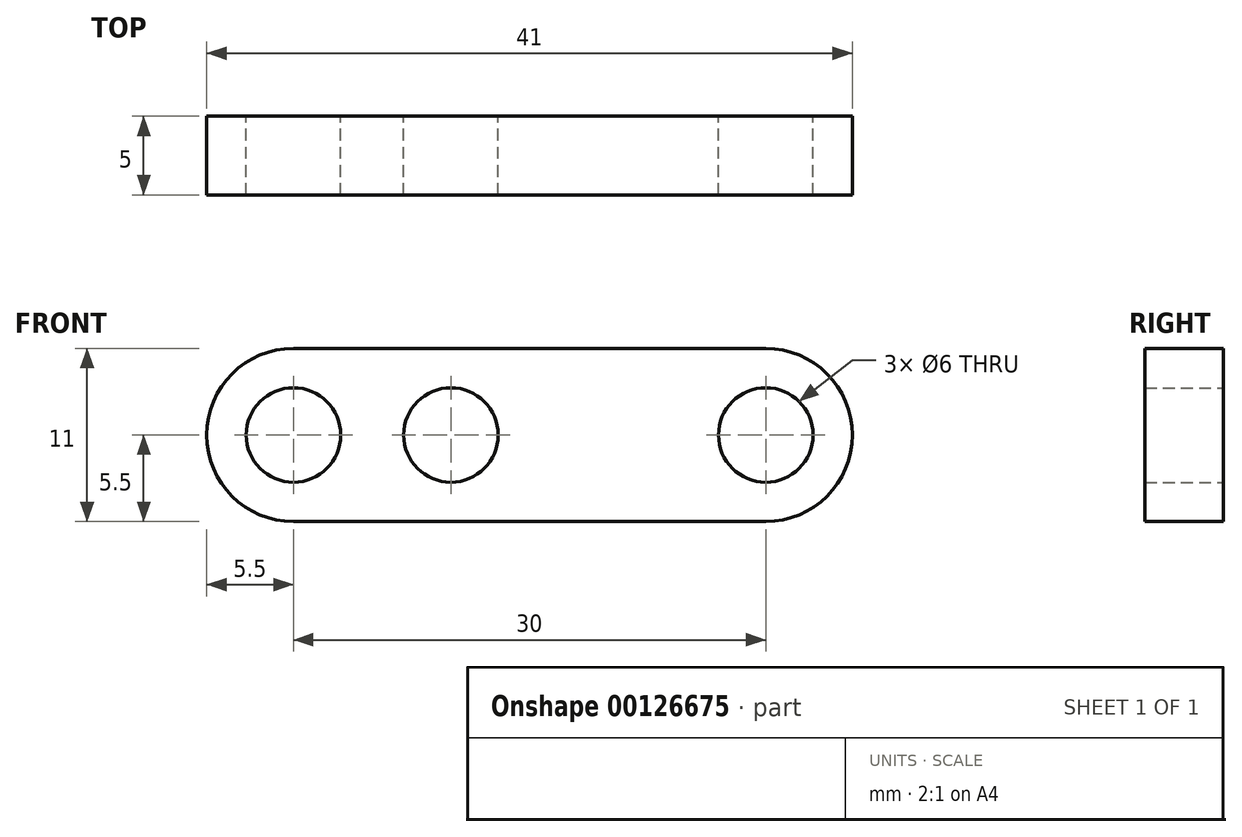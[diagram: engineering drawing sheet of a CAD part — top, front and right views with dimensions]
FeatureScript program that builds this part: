
annotation { "Feature Type Name" : "Feature", "Feature Type Description" : "" }
export const myFeature = defineFeature(function(context is Context, id is Id, definition is map)
    precondition{}
    {
        {
            var Q0;
            Q0=qCreatedBy(makeId("Front.planeOp"),FACE);
            var sketch = newSketch(context, id + "F0", { "sketchPlane" : qUnion([Q0])});
            skArc(sketch, "E0", {"start": v(0, 5.5) * mm, "mid": v(-5.5, 0) * mm, "end": v(0, -5.5) * mm});
            skCircle(sketch, "E1", {"center": v(0, 0) * mm, "radius": 3 * mm});
            skLineSegment(sketch, "E2", {"start": v(0, 5.5) * mm, "end": v(30, 5.5) * mm});
            skLineSegment(sketch, "E3", {"start": v(0, -5.5) * mm, "end": v(30, -5.5) * mm});
            skArc(sketch, "E4", {"start": v(30, -5.5) * mm, "mid": v(35.5, 0) * mm, "end": v(30, 5.5) * mm});
            skCircle(sketch, "E5", {"center": v(30, 0) * mm, "radius": 3 * mm});
            skCircle(sketch, "E6", {"center": v(10, 0) * mm, "radius": 3 * mm});
            skSolve(sketch);
        }
        {
            var Q0;
            Q0 = qSketchRegion(id + "F0", true);
            extrude(context, id + "F1", {"entities" : qUnion([Q0]), "depth" : 5 * mm});
        }
    });
